# Revit family: Faucet_Touchless-Lavatory-KOHLER-Loure-K-98454T_1
name_source: partatom
category: Plumbing Fixtures
units: mm (PartAtom-declared; Revit-internal decimal feet)

## family parameters
Cut with Voids When Loaded = No
Host = Face
OmniClass Number = 23.31.11.00
OmniClass Title = Faucets
Part Type = Normal
Room Calculation Point = No
Round Connector Dimension = Use Diameter
Shared = No

## types (3) — shared parameters
ADA Compliant = No
Apparent Load = 0 VA
Assembly Code = D2010
CW Connection = Yes
Cold Water Inlet = Cold Water Inlet
Date Modified = 12/13/2022
Default Elevation = 36"
Drain Included = Yes
Electrical Connector = Yes
Electrical Note = One Dedicated Circuit Required
Finish = Kohler-Metal-CP-Polished_Chrome
Flow Rate = 1 GPM
HW Connection = No
Height = 8 1/16"
Hot Water Inlet = Hot Water Inlet
Length = 4"
Manufacturer = Kohler Co.
Master Format 2014 = 22 41 39
Master Format 2014 Name = Residential Faucets, Supplies, and Trim
Material = Premium Metal Construction
Pressure = 0.00 psi
Product Name = Loure
Spout Reach = 4"
URL = http://www.kohler.com.cn
Vent Connection = No
Voltage = 220 V
Waste Connection = No
Waste Water Outlet = Waste Water Outlet
WaterSense Certified = No
Width = 2 7/16"

## per-type parameters (varying)
| type | Description | Model | Product Documentation Link | Product Page URL | Type |
| With Power Box, CP-Polished Chrome | Basin Induction Faucet AC (Single Cooling Type) | K-98454T-B-CP | https://files.kohler.com.cn | https://www.kohler.com.cn | 1 |
| Without Power Box, CP-Polished Chrome | Deck Mount Sensor Faucet Cold 0.5 GPM | K-98454T-NW-CP |  |  | 2 |
| CP-Polished Chrome | Deck Mount Sensor Faucet -AC | K-98454T-CP |  |  | 3 |

## geometry (parser evidence)
native form markers: Sweep x5
no freeform markers — native parametric forms only
